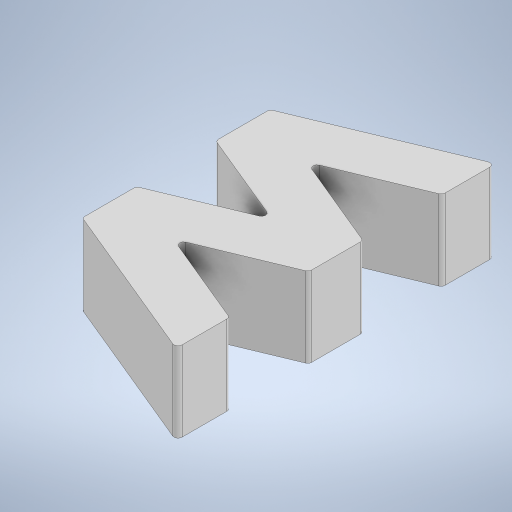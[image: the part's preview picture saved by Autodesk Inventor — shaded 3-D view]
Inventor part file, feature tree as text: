
AUTODESK INVENTOR PART (.ipt)
format: ipt  version: 2023 (Build 270158000, 158)  size: 303,616 bytes
history: native  units: mm
features: other x5, extrude x2, sketch x2, fillet x1, projected_geometry x1
ambient origin geometry x8: Origin, YZ Plane, XZ Plane, XY Plane, X Axis, Y Axis, Z Axis, Center Point
bodies: Body1 (feature_tree), Body2 (feature_tree)
feature tree (11):
  other  "contorno"
  extrude  "Extrusión1"  Depth=40.0mm
  fillet  "Empalme2"  Radius=20.0mm
  extrude  "Extrusión2"  Depth=10.0mm
  other  "Edición directa1"
  sketch  "Boceto1"  dims[d8=10.0mm d9=0.0mm d13=40.0mm d14=20.0mm]
  sketch  "Boceto2"  dims[d15=8.0mm d16=8.0mm d17=45.0deg d18=0.5mm d19=1.5mm d20=10.0mm d21=0.0mm d22=0.0mm d23=0.0mm d24=-1.5mm d25=0.0mm d26=0.0mm d27=-1.5mm]
  projected_geometry  "Contorno proyectado1"
  other  "cavidad"
  other  "Desplazar1"
  other  "Desplazar2"
